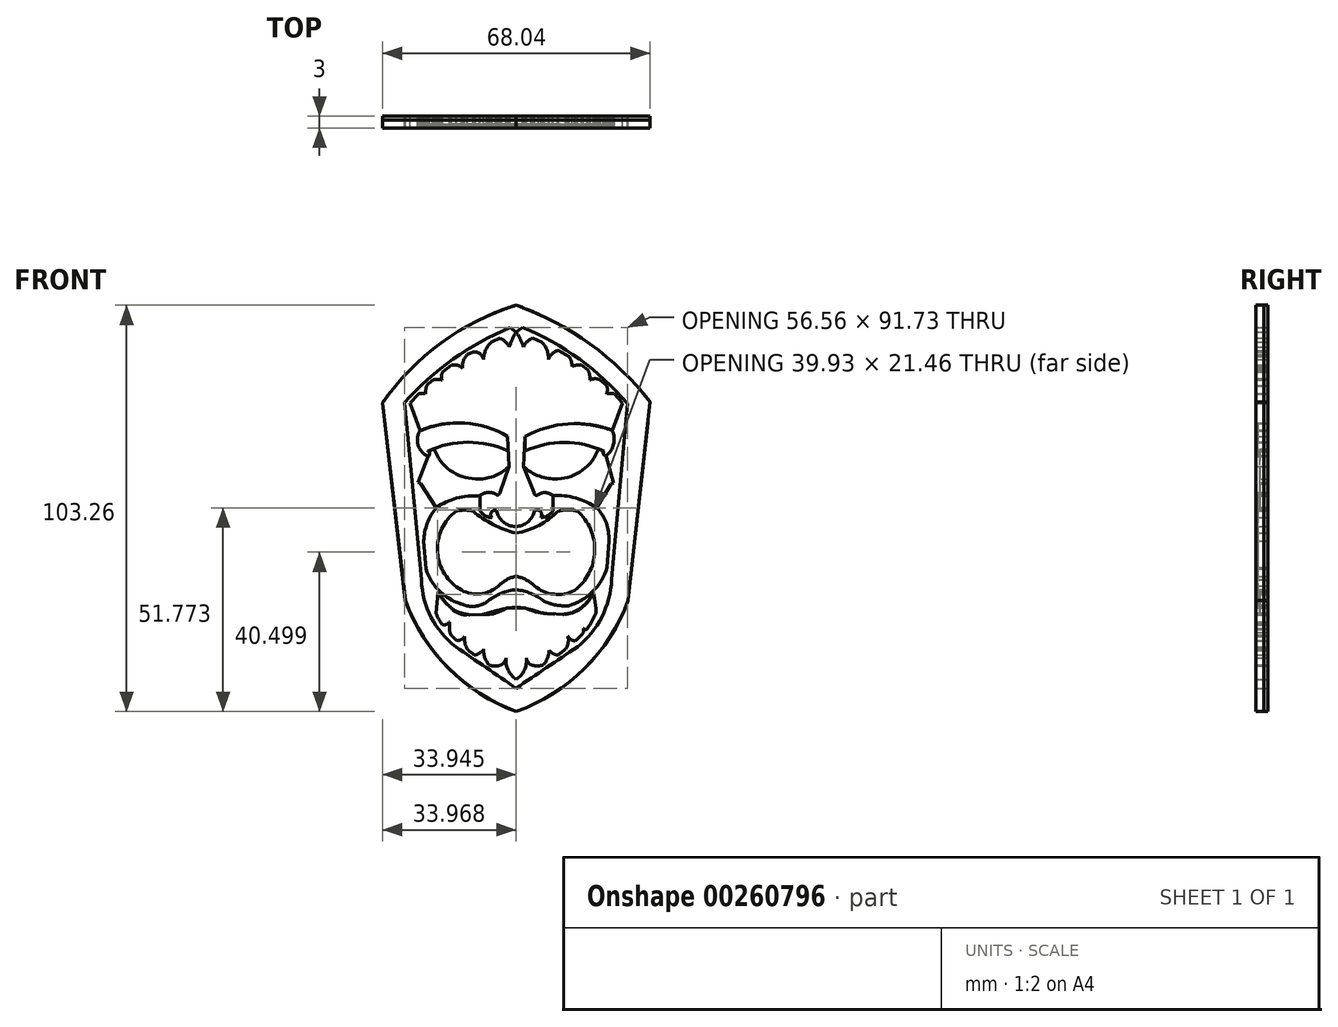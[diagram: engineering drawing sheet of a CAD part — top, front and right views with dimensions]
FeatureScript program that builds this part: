
annotation { "Feature Type Name" : "Feature", "Feature Type Description" : "" }
export const myFeature = defineFeature(function(context is Context, id is Id, definition is map)
    precondition{}
    {
        {
            var Q0;
            Q0=qCreatedBy(makeId("Front.planeOp"),FACE);
            var sketch = newSketch(context, id + "F0", { "sketchPlane" : qUnion([Q0])});
            skArc(sketch, "E0", {"start": v(34.06, 21.35) * mm, "mid": v(18.81, 36.12) * mm, "end": v(0, 45.95) * mm});
            skArc(sketch, "E1", {"start": v(0, 45.95) * mm, "mid": v(-19.06, 36.4) * mm, "end": v(-33.95, 21.15) * mm});
            skLineSegment(sketch, "E2", {"start": v(-33.95, 21.15) * mm, "end": v(-28.15, -29.05) * mm});
            skLineSegment(sketch, "E3", {"start": v(34.06, 21.35) * mm, "end": v(28.46, -29.05) * mm});
            skArc(sketch, "E4", {"start": v(-28.15, -29.05) * mm, "mid": v(-17.17, -46.24) * mm, "end": v(0, -57.26) * mm});
            skArc(sketch, "E5", {"start": v(0, -57.26) * mm, "mid": v(17.38, -46.33) * mm, "end": v(28.46, -29.05) * mm});
            skArc(sketch, "E6", {"start": v(-4.95, -6.25) * mm, "mid": v(-0.14, -10.26) * mm, "end": v(4.66, -6.25) * mm});
            skArc(sketch, "E7", {"start": v(-4.95, -6.25) * mm, "mid": v(-6.28, -6.6) * mm, "end": v(-6.16, -7.97) * mm});
            skArc(sketch, "E8", {"start": v(6.32, -7.94) * mm, "mid": v(6.17, -6.43) * mm, "end": v(4.66, -6.25) * mm});
            skArc(sketch, "E9", {"start": v(6.32, -7.94) * mm, "mid": v(8.06, -7.52) * mm, "end": v(9.33, -6.25) * mm});
            skArc(sketch, "E10", {"start": v(-9.24, -5.96) * mm, "mid": v(-8.02, -7.45) * mm, "end": v(-6.16, -7.97) * mm});
            skLineSegment(sketch, "E11", {"start": v(-9.24, -5.96) * mm, "end": v(-9.24, -2.5) * mm});
            skLineSegment(sketch, "E12", {"start": v(9.33, -6.25) * mm, "end": v(9.33, -2.5) * mm});
            skArc(sketch, "E13", {"start": v(-5.2, -2) * mm, "mid": v(-7.3, -1.58) * mm, "end": v(-9.24, -2.5) * mm});
            skArc(sketch, "E14", {"start": v(9.33, -2.5) * mm, "mid": v(7.6, -1.66) * mm, "end": v(5.72, -2.07) * mm});
            skArc(sketch, "E15", {"start": v(-5.2, -2) * mm, "mid": v(-4.5, -2.22) * mm, "end": v(-4.15, -1.58) * mm});
            skPoint(sketch, "E15.endSnap0", {"position": v(-7.3, -1.58) * mm});
            skArc(sketch, "E16", {"start": v(4.48, -1.6) * mm, "mid": v(4.93, -2.29) * mm, "end": v(5.72, -2.07) * mm});
            skLineSegment(sketch, "E17", {"start": v(-4.15, -1.58) * mm, "end": v(-1.86, 4.97) * mm});
            skLineSegment(sketch, "E18", {"start": v(4.48, -1.6) * mm, "end": v(1.89, 4.97) * mm});
            skLineSegment(sketch, "E19", {"start": v(1.89, 4.97) * mm, "end": v(3.01, 28.05) * mm});
            skLineSegment(sketch, "E20", {"start": v(-1.86, 4.97) * mm, "end": v(-2.83, 28.05) * mm});
            skArc(sketch, "E21", {"start": v(0, 39.14) * mm, "mid": v(-2.23, 33.8) * mm, "end": v(-2.83, 28.05) * mm});
            skArc(sketch, "E22", {"start": v(3.01, 28.05) * mm, "mid": v(2.38, 33.83) * mm, "end": v(0, 39.14) * mm});
            skArc(sketch, "E23", {"start": v(0, 39.14) * mm, "mid": v(-14.68, 31.95) * mm, "end": v(-26.96, 21.15) * mm});
            skArc(sketch, "E24", {"start": v(27.07, 21.15) * mm, "mid": v(14.78, 32.02) * mm, "end": v(0, 39.14) * mm});
            skArc(sketch, "E25", {"start": v(-18.2, -36.17) * mm, "mid": v(-9.75, -43.53) * mm, "end": v(0, -49.05) * mm});
            skArc(sketch, "E26", {"start": v(0, -49.05) * mm, "mid": v(9.75, -43.55) * mm, "end": v(18.15, -36.17) * mm});
            skArc(sketch, "E27", {"start": v(-22.54, -25.68) * mm, "mid": v(-20.91, -31.15) * mm, "end": v(-18.2, -36.17) * mm});
            skArc(sketch, "E28", {"start": v(18.15, -36.17) * mm, "mid": v(20.78, -31.11) * mm, "end": v(22.5, -25.68) * mm});
            skLineSegment(sketch, "E29", {"start": v(-26.96, 21.15) * mm, "end": v(-22.54, -25.68) * mm});
            skLineSegment(sketch, "E30", {"start": v(22.5, -25.68) * mm, "end": v(27.07, 21.15) * mm});
            skArc(sketch, "E31", {"start": v(-1.76, 35.38) * mm, "mid": v(-2.77, 36.68) * mm, "end": v(-4.14, 37.59) * mm});
            skArc(sketch, "E32", {"start": v(-6.23, 36.67) * mm, "mid": v(-7.72, 34.63) * mm, "end": v(-8.3, 32.17) * mm});
            skArc(sketch, "E33", {"start": v(4.2, 37.6) * mm, "mid": v(2.83, 36.72) * mm, "end": v(1.89, 35.38) * mm});
            skArc(sketch, "E34", {"start": v(8.18, 32.17) * mm, "mid": v(7.82, 34.58) * mm, "end": v(6.5, 36.63) * mm});
            skArc(sketch, "E35", {"start": v(10.73, 34.49) * mm, "mid": v(9.16, 33.65) * mm, "end": v(8.18, 32.17) * mm});
            skArc(sketch, "E36", {"start": v(14.13, 30.4) * mm, "mid": v(14.02, 31.7) * mm, "end": v(13.44, 32.88) * mm});
            skArc(sketch, "E37", {"start": v(-12.43, 33.38) * mm, "mid": v(-13.4, 31.84) * mm, "end": v(-13.67, 30.04) * mm});
            skArc(sketch, "E38", {"start": v(-8.3, 32.17) * mm, "mid": v(-9.23, 33.64) * mm, "end": v(-10.91, 34.08) * mm});
            skArc(sketch, "E39", {"start": v(-13.67, 30.04) * mm, "mid": v(-14.96, 30.72) * mm, "end": v(-16.41, 30.75) * mm});
            skArc(sketch, "E40", {"start": v(16.61, 30.75) * mm, "mid": v(15.34, 30.75) * mm, "end": v(14.13, 30.4) * mm});
            skArc(sketch, "E41", {"start": v(18.72, 26.93) * mm, "mid": v(18.67, 28.23) * mm, "end": v(18.3, 29.49) * mm});
            skArc(sketch, "E42", {"start": v(21.38, 26.93) * mm, "mid": v(20.05, 27.3) * mm, "end": v(18.72, 26.93) * mm});
            skArc(sketch, "E43", {"start": v(22.97, 23.47) * mm, "mid": v(23.18, 24.43) * mm, "end": v(23.05, 25.4) * mm});
            skArc(sketch, "E44", {"start": v(24.97, 23.47) * mm, "mid": v(23.97, 23.54) * mm, "end": v(22.97, 23.47) * mm});
            skArc(sketch, "E45", {"start": v(-18.68, 29.04) * mm, "mid": v(-18.98, 28) * mm, "end": v(-18.84, 26.93) * mm});
            skArc(sketch, "E46", {"start": v(-18.84, 26.93) * mm, "mid": v(-20.02, 27.15) * mm, "end": v(-21.2, 26.93) * mm});
            skArc(sketch, "E47", {"start": v(-22.77, 25.5) * mm, "mid": v(-22.94, 24.5) * mm, "end": v(-23, 23.47) * mm});
            skArc(sketch, "E48", {"start": v(-23, 23.47) * mm, "mid": v(-23.92, 23.54) * mm, "end": v(-24.84, 23.47) * mm});
            skLineSegment(sketch, "E49", {"start": v(-8.3, 32.17) * mm, "end": v(-6.65, 14.76) * mm});
            skLineSegment(sketch, "E50", {"start": v(-13.67, 30.04) * mm, "end": v(-11.48, 15.83) * mm});
            skLineSegment(sketch, "E51", {"start": v(-18.84, 26.93) * mm, "end": v(-16.08, 15.97) * mm});
            skLineSegment(sketch, "E52", {"start": v(-23, 23.47) * mm, "end": v(-19.76, 15.55) * mm});
            skLineSegment(sketch, "E53", {"start": v(-26.96, 21.15) * mm, "end": v(-24.42, 14.13) * mm});
            skLineSegment(sketch, "E54", {"start": v(8.18, 32.17) * mm, "end": v(6.26, 14.4) * mm});
            skLineSegment(sketch, "E55", {"start": v(14.13, 30.4) * mm, "end": v(11.16, 15.6) * mm});
            skLineSegment(sketch, "E56", {"start": v(18.72, 26.93) * mm, "end": v(15.97, 15.87) * mm});
            skLineSegment(sketch, "E57", {"start": v(22.97, 23.47) * mm, "end": v(20.08, 15.43) * mm});
            skLineSegment(sketch, "E58", {"start": v(27.07, 21.15) * mm, "end": v(24.52, 14.2) * mm});
            skArc(sketch, "E59", {"start": v(-2.18, 12.64) * mm, "mid": v(-13.13, 16) * mm, "end": v(-24.42, 14.13) * mm});
            skArc(sketch, "E60", {"start": v(24.52, 14.2) * mm, "mid": v(13.22, 15.82) * mm, "end": v(2.26, 12.63) * mm});
            skLineSegment(sketch, "E61", {"start": v(-19.8, -26.85) * mm, "end": v(-20.4, -32.31) * mm});
            skLineSegment(sketch, "E62", {"start": v(-16.98, -30.48) * mm, "end": v(-16.98, -36.07) * mm});
            skArc(sketch, "E63", {"start": v(-16.98, -36.07) * mm, "mid": v(-16.88, -36.96) * mm, "end": v(-16.6, -37.8) * mm});
            skArc(sketch, "E64", {"start": v(-15.13, -39.2) * mm, "mid": v(-13.97, -39) * mm, "end": v(-13.1, -38.2) * mm});
            skLineSegment(sketch, "E65", {"start": v(-13.1, -38.2) * mm, "end": v(-12.59, -32.7) * mm});
            skArc(sketch, "E66", {"start": v(-13.1, -38.2) * mm, "mid": v(-12.99, -39.95) * mm, "end": v(-12.34, -41.58) * mm});
            skArc(sketch, "E67", {"start": v(-10.57, -42.94) * mm, "mid": v(-9.24, -42.41) * mm, "end": v(-8.23, -41.4) * mm});
            skLineSegment(sketch, "E68", {"start": v(-8.23, -41.4) * mm, "end": v(-7.66, -32.61) * mm});
            skLineSegment(sketch, "E69", {"start": v(-7.66, -32.61) * mm, "end": v(-12.59, -32.7) * mm});
            skArc(sketch, "E70", {"start": v(-19.8, -26.85) * mm, "mid": v(-18.63, -28.85) * mm, "end": v(-16.98, -30.48) * mm});
            skArc(sketch, "E71", {"start": v(-16.98, -30.48) * mm, "mid": v(-15.06, -32.14) * mm, "end": v(-12.59, -32.7) * mm});
            skArc(sketch, "E72", {"start": v(-7.66, -32.61) * mm, "mid": v(-4.85, -32.15) * mm, "end": v(-2.3, -30.9) * mm});
            skLineSegment(sketch, "E73", {"start": v(-2.3, -30.9) * mm, "end": v(2.2, -30.9) * mm});
            skArc(sketch, "E74", {"start": v(2.2, -30.9) * mm, "mid": v(4.96, -31.92) * mm, "end": v(7.88, -32.38) * mm});
            skLineSegment(sketch, "E75", {"start": v(7.88, -32.38) * mm, "end": v(12.54, -32.64) * mm});
            skArc(sketch, "E76", {"start": v(12.54, -32.64) * mm, "mid": v(16.9, -30.74) * mm, "end": v(19.69, -26.9) * mm});
            skLineSegment(sketch, "E77", {"start": v(19.69, -26.9) * mm, "end": v(20.28, -31.01) * mm});
            skArc(sketch, "E78", {"start": v(20.28, -32.26) * mm, "mid": v(20.33, -31.64) * mm, "end": v(20.28, -31.01) * mm});
            skArc(sketch, "E79", {"start": v(17.15, -36.17) * mm, "mid": v(17.65, -36.47) * mm, "end": v(18.15, -36.17) * mm});
            skArc(sketch, "E80", {"start": v(13.1, -38.04) * mm, "mid": v(13.86, -38.97) * mm, "end": v(15, -39.3) * mm});
            skArc(sketch, "E81", {"start": v(12.7, -41.3) * mm, "mid": v(13.23, -39.71) * mm, "end": v(13.1, -38.04) * mm});
            skArc(sketch, "E82", {"start": v(8.39, -41.7) * mm, "mid": v(9.37, -42.55) * mm, "end": v(10.6, -42.94) * mm});
            skArc(sketch, "E83", {"start": v(6.97, -45.4) * mm, "mid": v(7.95, -43.66) * mm, "end": v(8.39, -41.7) * mm});
            skLineSegment(sketch, "E84", {"start": v(13.1, -38.04) * mm, "end": v(12.54, -32.64) * mm});
            skLineSegment(sketch, "E85", {"start": v(17.15, -36.17) * mm, "end": v(16.9, -30.74) * mm});
            skLineSegment(sketch, "E86", {"start": v(17.15, -36.17) * mm, "end": v(17.15, -37.22) * mm});
            skArc(sketch, "E87", {"start": v(3.8, -45.4) * mm, "mid": v(5.38, -45.7) * mm, "end": v(6.97, -45.4) * mm});
            skArc(sketch, "E88", {"start": v(2.59, -43.7) * mm, "mid": v(3, -44.68) * mm, "end": v(3.8, -45.4) * mm});
            skArc(sketch, "E89", {"start": v(0, -49.05) * mm, "mid": v(2.1, -46.76) * mm, "end": v(2.59, -43.7) * mm});
            skArc(sketch, "E90", {"start": v(-2.58, -43.7) * mm, "mid": v(-2.04, -46.73) * mm, "end": v(0, -49.05) * mm});
            skArc(sketch, "E91", {"start": v(-3.72, -45.37) * mm, "mid": v(-2.96, -44.66) * mm, "end": v(-2.58, -43.7) * mm});
            skArc(sketch, "E92", {"start": v(-7, -45.37) * mm, "mid": v(-5.36, -45.72) * mm, "end": v(-3.72, -45.37) * mm});
            skArc(sketch, "E93", {"start": v(-8.23, -41.4) * mm, "mid": v(-7.98, -43.5) * mm, "end": v(-7, -45.37) * mm});
            skLineSegment(sketch, "E94", {"start": v(-2.58, -43.7) * mm, "end": v(-2.3, -30.9) * mm});
            skLineSegment(sketch, "E95", {"start": v(2.59, -43.7) * mm, "end": v(2.2, -30.9) * mm});
            skLineSegment(sketch, "E96", {"start": v(8.39, -41.7) * mm, "end": v(7.88, -32.38) * mm});
            skArc(sketch, "E97", {"start": v(0, -51.37) * mm, "mid": v(-7.64, -46.1) * mm, "end": v(-15.29, -40.85) * mm});
            skArc(sketch, "E98", {"start": v(15.54, -40.85) * mm, "mid": v(7.76, -46.1) * mm, "end": v(0, -51.37) * mm});
            skArc(sketch, "E99", {"start": v(-24.05, -23.86) * mm, "mid": v(-21.6, -33.35) * mm, "end": v(-15.29, -40.85) * mm});
            skArc(sketch, "E100", {"start": v(15.54, -40.85) * mm, "mid": v(21.77, -33.25) * mm, "end": v(24.24, -23.74) * mm});
            skLineSegment(sketch, "E101", {"start": v(-28.32, 21.26) * mm, "end": v(-24.05, -23.86) * mm});
            skLineSegment(sketch, "E102", {"start": v(28.25, 21) * mm, "end": v(24.24, -23.74) * mm});
            skArc(sketch, "E103", {"start": v(-1.57, 40.24) * mm, "mid": v(-16.02, 32.26) * mm, "end": v(-28.32, 21.26) * mm});
            skArc(sketch, "E104", {"start": v(28.25, 21) * mm, "mid": v(16.05, 32.24) * mm, "end": v(1.6, 40.36) * mm});
            skLineSegment(sketch, "E105", {"start": v(0, 39.14) * mm, "end": v(-1.57, 40.24) * mm});
            skLineSegment(sketch, "E106", {"start": v(0, 39.14) * mm, "end": v(1.6, 40.36) * mm});
            skLineSegment(sketch, "E107", {"start": v(-26.96, 21.15) * mm, "end": v(-24.84, 23.47) * mm});
            skLineSegment(sketch, "E108", {"start": v(-22.77, 25.5) * mm, "end": v(-21.2, 26.93) * mm});
            skLineSegment(sketch, "E109", {"start": v(-18.68, 29.04) * mm, "end": v(-16.41, 30.75) * mm});
            skLineSegment(sketch, "E110", {"start": v(-12.43, 33.38) * mm, "end": v(-10.91, 34.08) * mm});
            skLineSegment(sketch, "E111", {"start": v(-6.23, 36.67) * mm, "end": v(-4.14, 37.59) * mm});
            skLineSegment(sketch, "E112", {"start": v(4.2, 37.6) * mm, "end": v(6.5, 36.63) * mm});
            skLineSegment(sketch, "E113", {"start": v(10.73, 34.49) * mm, "end": v(13.44, 32.88) * mm});
            skLineSegment(sketch, "E114", {"start": v(16.61, 30.75) * mm, "end": v(18.3, 29.49) * mm});
            skLineSegment(sketch, "E115", {"start": v(21.38, 26.93) * mm, "end": v(23.05, 25.4) * mm});
            skLineSegment(sketch, "E116", {"start": v(24.97, 23.47) * mm, "end": v(27.07, 21.15) * mm});
            skArc(sketch, "E117", {"start": v(-18.91, -35.05) * mm, "mid": v(-17.83, -35.18) * mm, "end": v(-16.98, -34.49) * mm});
            skSolve(sketch);
        }
        {
            var Q0;
            Q0=qCreatedBy(makeId("Front.planeOp"),FACE);
            var sketch = newSketch(context, id + "F1", { "sketchPlane" : qUnion([Q0])});
            skArc(sketch, "E118", {"start": v(-2.16, 12.64) * mm, "mid": v(-13.16, 16) * mm, "end": v(-24.48, 14) * mm});
            skArc(sketch, "E119", {"start": v(24.36, 14.13) * mm, "mid": v(13.13, 15.82) * mm, "end": v(2.23, 12.64) * mm});
            skArc(sketch, "E120", {"start": v(22.87, 7.79) * mm, "mid": v(24.77, 10.69) * mm, "end": v(24.36, 14.13) * mm});
            skArc(sketch, "E121", {"start": v(-24.48, 14) * mm, "mid": v(-24.87, 10.32) * mm, "end": v(-22.4, 7.58) * mm});
            skArc(sketch, "E122", {"start": v(-22.4, 7.58) * mm, "mid": v(-21.99, 8.22) * mm, "end": v(-22.4, 8.86) * mm});
            skArc(sketch, "E123", {"start": v(22.27, 8.86) * mm, "mid": v(22.21, 8.13) * mm, "end": v(22.87, 7.79) * mm});
            skArc(sketch, "E124", {"start": v(22.27, 8.86) * mm, "mid": v(12.25, 11.1) * mm, "end": v(2.23, 8.86) * mm});
            skArc(sketch, "E125", {"start": v(-1.95, 8.86) * mm, "mid": v(-12.17, 11.15) * mm, "end": v(-22.4, 8.86) * mm});
            skArc(sketch, "E126", {"start": v(-9.37, -2.54) * mm, "mid": v(-15.1, -3.05) * mm, "end": v(-20.3, -5.5) * mm});
            skArc(sketch, "E127", {"start": v(20.51, -5.57) * mm, "mid": v(15.15, -3.03) * mm, "end": v(9.25, -2.4) * mm});
            skArc(sketch, "E128", {"start": v(23.55, -13.87) * mm, "mid": v(22.9, -9.4) * mm, "end": v(20.51, -5.57) * mm});
            skArc(sketch, "E129", {"start": v(-20.3, -5.5) * mm, "mid": v(-22.6, -9.45) * mm, "end": v(-23.47, -13.94) * mm});
            skLineSegment(sketch, "E130", {"start": v(-23.47, -13.94) * mm, "end": v(-22.95, -21.1) * mm});
            skLineSegment(sketch, "E131", {"start": v(23.55, -13.87) * mm, "end": v(23.13, -20.68) * mm});
            skArc(sketch, "E132", {"start": v(-22.95, -21.1) * mm, "mid": v(-19.25, -26.83) * mm, "end": v(-13.3, -30.17) * mm});
            skArc(sketch, "E133", {"start": v(13.29, -30.39) * mm, "mid": v(19.46, -26.8) * mm, "end": v(23.13, -20.68) * mm});
            skArc(sketch, "E134", {"start": v(-13.3, -30.17) * mm, "mid": v(-10.14, -30.49) * mm, "end": v(-7.22, -29.24) * mm});
            skArc(sketch, "E135", {"start": v(7.14, -29.24) * mm, "mid": v(10.14, -30.22) * mm, "end": v(13.29, -30.39) * mm});
            skArc(sketch, "E136", {"start": v(0, -26.31) * mm, "mid": v(-3.83, -27.25) * mm, "end": v(-7.22, -29.24) * mm});
            skArc(sketch, "E137", {"start": v(7.14, -29.24) * mm, "mid": v(3.78, -27.28) * mm, "end": v(0, -26.31) * mm});
            skLineSegment(sketch, "E138", {"start": v(-9.37, -2.54) * mm, "end": v(-9.24, -2.55) * mm});
            skLineSegment(sketch, "E139", {"start": v(-9.24, -2.55) * mm, "end": v(-9.24, -5.94) * mm});
            skLineSegment(sketch, "E140", {"start": v(9.25, -2.4) * mm, "end": v(9.25, -6.32) * mm});
            skArc(sketch, "E141", {"start": v(-9.24, -5.94) * mm, "mid": v(-8.03, -7.45) * mm, "end": v(-6.16, -7.94) * mm});
            skArc(sketch, "E142", {"start": v(6.33, -7.93) * mm, "mid": v(8, -7.52) * mm, "end": v(9.25, -6.32) * mm});
            skArc(sketch, "E143", {"start": v(-4.95, -6.24) * mm, "mid": v(-6.26, -6.59) * mm, "end": v(-6.16, -7.94) * mm});
            skArc(sketch, "E144", {"start": v(6.33, -7.93) * mm, "mid": v(6.15, -6.43) * mm, "end": v(4.65, -6.24) * mm});
            skArc(sketch, "E145", {"start": v(-4.95, -6.24) * mm, "mid": v(-0.14, -10.24) * mm, "end": v(4.65, -6.24) * mm});
            skArc(sketch, "E146", {"start": v(-15.24, -6.32) * mm, "mid": v(-19.98, -16.74) * mm, "end": v(-13.9, -26.43) * mm});
            skArc(sketch, "E147", {"start": v(14.84, -26.5) * mm, "mid": v(19.96, -16.57) * mm, "end": v(15.52, -6.32) * mm});
            skArc(sketch, "E148", {"start": v(15.52, -6.32) * mm, "mid": v(13.12, -6.05) * mm, "end": v(10.73, -6.32) * mm});
            skArc(sketch, "E149", {"start": v(-11, -6.32) * mm, "mid": v(-13.12, -6.1) * mm, "end": v(-15.24, -6.32) * mm});
            skArc(sketch, "E150", {"start": v(-11, -6.32) * mm, "mid": v(-5.82, -9.76) * mm, "end": v(0, -11.92) * mm});
            skArc(sketch, "E151", {"start": v(0, -11.92) * mm, "mid": v(5.8, -9.95) * mm, "end": v(10.73, -6.32) * mm});
            skArc(sketch, "E152", {"start": v(-13.9, -26.43) * mm, "mid": v(-9, -27.35) * mm, "end": v(-4.45, -25.35) * mm});
            skArc(sketch, "E153", {"start": v(4.66, -25.35) * mm, "mid": v(9.58, -27.46) * mm, "end": v(14.84, -26.5) * mm});
            skArc(sketch, "E154", {"start": v(4.66, -25.35) * mm, "mid": v(2.5, -23.79) * mm, "end": v(0, -22.92) * mm});
            skArc(sketch, "E155", {"start": v(0, -22.92) * mm, "mid": v(-2.42, -23.78) * mm, "end": v(-4.45, -25.35) * mm});
            skLineSegment(sketch, "E156", {"start": v(-1.95, 8.86) * mm, "end": v(-2.16, 12.64) * mm});
            skLineSegment(sketch, "E157", {"start": v(2.23, 12.64) * mm, "end": v(2.23, 8.86) * mm});
            skSolve(sketch);
        }
        {
            var Q0;
            Q0=qCreatedBy(makeId("Front.planeOp"),FACE);
            var sketch = newSketch(context, id + "F2", { "sketchPlane" : qUnion([Q0])});
            skLineSegment(sketch, "E158", {"start": v(-20.36, -5.45) * mm, "end": v(-24.3, 0.63) * mm});
            skLineSegment(sketch, "E159", {"start": v(-24.3, 0.63) * mm, "end": v(-24.98, 0.95) * mm});
            skLineSegment(sketch, "E160", {"start": v(-24.98, 0.95) * mm, "end": v(-22.37, 7.54) * mm});
            skLineSegment(sketch, "E161", {"start": v(20.46, -5.55) * mm, "end": v(24.08, 0.5) * mm});
            skLineSegment(sketch, "E162", {"start": v(24.08, 0.5) * mm, "end": v(24.69, 0.82) * mm});
            skLineSegment(sketch, "E163", {"start": v(24.69, 0.82) * mm, "end": v(22.81, 7.73) * mm});
            skArc(sketch, "E164", {"start": v(22.24, 8.87) * mm, "mid": v(22.17, 8.12) * mm, "end": v(22.81, 7.73) * mm});
            skArc(sketch, "E165", {"start": v(-22.37, 7.54) * mm, "mid": v(-21.99, 8.18) * mm, "end": v(-22.37, 8.83) * mm});
            skArc(sketch, "E166", {"start": v(-9.3, -2.5) * mm, "mid": v(-15.07, -3.07) * mm, "end": v(-20.36, -5.45) * mm});
            skArc(sketch, "E167", {"start": v(20.46, -5.55) * mm, "mid": v(15.13, -3.08) * mm, "end": v(9.29, -2.44) * mm});
            skArc(sketch, "E168", {"start": v(9.29, -2.44) * mm, "mid": v(7.57, -1.65) * mm, "end": v(5.72, -2.07) * mm});
            skArc(sketch, "E169", {"start": v(4.49, -1.6) * mm, "mid": v(4.93, -2.3) * mm, "end": v(5.72, -2.07) * mm});
            skArc(sketch, "E170", {"start": v(-5.2, -2) * mm, "mid": v(-7.33, -1.6) * mm, "end": v(-9.3, -2.5) * mm});
            skArc(sketch, "E171", {"start": v(-5.2, -2) * mm, "mid": v(-4.5, -2.22) * mm, "end": v(-4.15, -1.59) * mm});
            skArc(sketch, "E172", {"start": v(1.9, 4.98) * mm, "mid": v(5.9, 2.53) * mm, "end": v(10.54, 1.85) * mm});
            skArc(sketch, "E173", {"start": v(10.54, 1.85) * mm, "mid": v(16.88, 4.06) * mm, "end": v(20.87, 9.44) * mm});
            skArc(sketch, "E174", {"start": v(-10.29, 1.85) * mm, "mid": v(-5.74, 2.5) * mm, "end": v(-1.86, 4.98) * mm});
            skArc(sketch, "E175", {"start": v(-20.86, 9.46) * mm, "mid": v(-16.76, 4.01) * mm, "end": v(-10.29, 1.85) * mm});
            skLineSegment(sketch, "E176", {"start": v(-22.37, 8.83) * mm, "end": v(-20.86, 9.46) * mm});
            skLineSegment(sketch, "E177", {"start": v(20.87, 9.44) * mm, "end": v(22.24, 8.87) * mm});
            skLineSegment(sketch, "E178", {"start": v(4.49, -1.6) * mm, "end": v(1.9, 4.98) * mm});
            skLineSegment(sketch, "E179", {"start": v(-1.86, 4.98) * mm, "end": v(-4.15, -1.59) * mm});
            skArc(sketch, "E180", {"start": v(-13.42, -32.37) * mm, "mid": v(-10.45, -32.78) * mm, "end": v(-7.48, -32.37) * mm});
            skArc(sketch, "E181", {"start": v(0, -30.76) * mm, "mid": v(-3.79, -31.36) * mm, "end": v(-7.48, -32.37) * mm});
            skArc(sketch, "E182", {"start": v(6.74, -32.37) * mm, "mid": v(3.43, -31.32) * mm, "end": v(0, -30.76) * mm});
            skArc(sketch, "E183", {"start": v(6.74, -32.37) * mm, "mid": v(9.97, -32.68) * mm, "end": v(13.2, -32.37) * mm});
            skArc(sketch, "E184", {"start": v(13.2, -32.37) * mm, "mid": v(17.15, -30.34) * mm, "end": v(19.64, -26.66) * mm});
            skArc(sketch, "E185", {"start": v(13.3, -30.38) * mm, "mid": v(16.72, -28.95) * mm, "end": v(19.64, -26.66) * mm});
            skArc(sketch, "E186", {"start": v(7.14, -29.26) * mm, "mid": v(10.15, -30.21) * mm, "end": v(13.3, -30.38) * mm});
            skArc(sketch, "E187", {"start": v(7.14, -29.26) * mm, "mid": v(3.78, -27.28) * mm, "end": v(0, -26.31) * mm});
            skArc(sketch, "E188", {"start": v(0, -26.31) * mm, "mid": v(-3.84, -27.25) * mm, "end": v(-7.23, -29.26) * mm});
            skArc(sketch, "E189", {"start": v(-13.3, -30.17) * mm, "mid": v(-10.15, -30.5) * mm, "end": v(-7.23, -29.26) * mm});
            skArc(sketch, "E190", {"start": v(-19.4, -26.68) * mm, "mid": v(-17.2, -30.36) * mm, "end": v(-13.42, -32.37) * mm});
            skArc(sketch, "E191", {"start": v(-19.4, -26.68) * mm, "mid": v(-16.58, -28.83) * mm, "end": v(-13.3, -30.17) * mm});
            skSolve(sketch);
        }
        {
            var Q0;
            Q0=makeQuery(id+"F2.imprint","IMPRINT",FACE,{"disambiguationData":[TD([[makeQuery(id+"F2.imprint","IMPRINT",EDGE,{"derivedFrom":sQuery(id+"F2.wireOp",EDGE,"E158")}),-1.0]])]});
            var Q1;
            Q1=makeQuery(id+"F2.imprint","IMPRINT",FACE,{"disambiguationData":[TD([[makeQuery(id+"F2.imprint","IMPRINT",EDGE,{"derivedFrom":sQuery(id+"F2.wireOp",EDGE,"E161")}),1.0]])]});
            var Q2;
            Q2=makeQuery(id+"F2.imprint","IMPRINT",FACE,{"disambiguationData":[TD([[makeQuery(id+"F2.imprint","IMPRINT",EDGE,{"derivedFrom":sQuery(id+"F2.wireOp",EDGE,"E180")}),1.0]])]});
            extrude(context, id + "F3", {"entities" : qUnion([Q0, Q1, Q2]), "depth" : 2 * mm});
        }
        {
            var Q0;
            Q0=makeQuery(id+"F1.imprint","IMPRINT",FACE,{"disambiguationData":[TD([[makeQuery(id+"F1.imprint","IMPRINT",EDGE,{"derivedFrom":sQuery(id+"F1.wireOp",EDGE,"E126")}),1.0]])]});
            var Q1;
            Q1=makeQuery(id+"F1.imprint","IMPRINT",FACE,{"disambiguationData":[TD([[makeQuery(id+"F1.imprint","IMPRINT",EDGE,{"derivedFrom":sQuery(id+"F1.wireOp",EDGE,"E119")}),1.0]])]});
            var Q2;
            Q2=makeQuery(id+"F1.imprint","IMPRINT",FACE,{"disambiguationData":[TD([[makeQuery(id+"F1.imprint","IMPRINT",EDGE,{"derivedFrom":sQuery(id+"F1.wireOp",EDGE,"E118")}),1.0]])]});
            extrude(context, id + "F4", {"entities" : qUnion([Q0, Q1, Q2]), "depth" : 2.5 * mm});
        }
        {
            var Q0;
            Q0=makeQuery(id+"F0.imprint","IMPRINT",FACE,{"disambiguationData":[TD([[makeQuery(id+"F0.imprint","IMPRINT",EDGE,{"derivedFrom":sQuery(id+"F0.wireOp",EDGE,"E6")}),1.0]])]});
            var Q1;
            {var subQ3=sQuery(id+"F0.wireOp",EDGE,"E31");Q1=makeQuery(id+"F0.imprint","IMPRINT",FACE,{"disambiguationData":[TD([[makeQuery(id+"F0.imprint","IMPRINT",EDGE,{"derivedFrom":subQ3}),1.0]])]});}
            var Q2;
            {var subQ5=sQuery(id+"F0.wireOp",EDGE,"E39");Q2=makeQuery(id+"F0.imprint","IMPRINT",FACE,{"disambiguationData":[TD([[makeQuery(id+"F0.imprint","IMPRINT",EDGE,{"derivedFrom":subQ5}),1.0]])]});}
            var Q3;
            {var subQ5=sQuery(id+"F0.wireOp",EDGE,"E46");Q3=makeQuery(id+"F0.imprint","IMPRINT",FACE,{"disambiguationData":[TD([[makeQuery(id+"F0.imprint","IMPRINT",EDGE,{"derivedFrom":subQ5}),1.0]])]});}
            var Q4;
            {var subQ4=sQuery(id+"F0.wireOp",EDGE,"E48");Q4=makeQuery(id+"F0.imprint","IMPRINT",FACE,{"disambiguationData":[TD([[makeQuery(id+"F0.imprint","IMPRINT",EDGE,{"derivedFrom":subQ4}),1.0]])]});}
            var Q5;
            {var subQ0=sQuery(id+"F0.wireOp",EDGE,"E33");Q5=makeQuery(id+"F0.imprint","IMPRINT",FACE,{"disambiguationData":[TD([[makeQuery(id+"F0.imprint","IMPRINT",EDGE,{"derivedFrom":subQ0}),1.0]])]});}
            var Q6;
            Q6=makeQuery(id+"F0.imprint","IMPRINT",FACE,{"disambiguationData":[TD([[makeQuery(id+"F0.imprint","IMPRINT",EDGE,{"derivedFrom":sQuery(id+"F0.wireOp",EDGE,"E35")}),1.0]])]});
            var Q7;
            Q7=makeQuery(id+"F0.imprint","IMPRINT",FACE,{"disambiguationData":[TD([[makeQuery(id+"F0.imprint","IMPRINT",EDGE,{"derivedFrom":sQuery(id+"F0.wireOp",EDGE,"E40")}),1.0]])]});
            var Q8;
            Q8=makeQuery(id+"F0.imprint","IMPRINT",FACE,{"disambiguationData":[TD([[makeQuery(id+"F0.imprint","IMPRINT",EDGE,{"derivedFrom":sQuery(id+"F0.wireOp",EDGE,"E42")}),1.0]])]});
            var Q9;
            Q9=makeQuery(id+"F0.imprint","IMPRINT",FACE,{"disambiguationData":[TD([[makeQuery(id+"F0.imprint","IMPRINT",EDGE,{"derivedFrom":sQuery(id+"F0.wireOp",EDGE,"E44")}),1.0]])]});
            var Q10;
            {var subQ1=sQuery(id+"F0.wireOp",EDGE,"E61");Q10=makeQuery(id+"F0.imprint","IMPRINT",FACE,{"disambiguationData":[TD([[makeQuery(id+"F0.imprint","IMPRINT",EDGE,{"derivedFrom":subQ1}),1.0]])]});}
            var Q11;
            {var subQ0=sQuery(id+"F0.wireOp",EDGE,"E63");Q11=makeQuery(id+"F0.imprint","IMPRINT",FACE,{"disambiguationData":[TD([[makeQuery(id+"F0.imprint","IMPRINT",EDGE,{"derivedFrom":subQ0}),1.0]])]});}
            var Q12;
            Q12=makeQuery(id+"F0.imprint","IMPRINT",FACE,{"disambiguationData":[TD([[makeQuery(id+"F0.imprint","IMPRINT",EDGE,{"derivedFrom":sQuery(id+"F0.wireOp",EDGE,"E65")}),-1.0]])]});
            var Q13;
            Q13=makeQuery(id+"F0.imprint","IMPRINT",FACE,{"disambiguationData":[TD([[makeQuery(id+"F0.imprint","IMPRINT",EDGE,{"derivedFrom":sQuery(id+"F0.wireOp",EDGE,"E68")}),-1.0]])]});
            var Q14;
            Q14=makeQuery(id+"F0.imprint","IMPRINT",FACE,{"disambiguationData":[TD([[makeQuery(id+"F0.imprint","IMPRINT",EDGE,{"derivedFrom":sQuery(id+"F0.wireOp",EDGE,"E73")}),-1.0]])]});
            var Q15;
            Q15=makeQuery(id+"F0.imprint","IMPRINT",FACE,{"disambiguationData":[TD([[makeQuery(id+"F0.imprint","IMPRINT",EDGE,{"derivedFrom":sQuery(id+"F0.wireOp",EDGE,"E74")}),-1.0]])]});
            var Q16;
            Q16=makeQuery(id+"F0.imprint","IMPRINT",FACE,{"disambiguationData":[TD([[makeQuery(id+"F0.imprint","IMPRINT",EDGE,{"derivedFrom":sQuery(id+"F0.wireOp",EDGE,"E75")}),-1.0]])]});
            var Q17;
            {var subQ1=sQuery(id+"F0.wireOp",EDGE,"E80");Q17=makeQuery(id+"F0.imprint","IMPRINT",FACE,{"disambiguationData":[TD([[makeQuery(id+"F0.imprint","IMPRINT",EDGE,{"derivedFrom":subQ1}),1.0]])]});}
            var Q18;
            {var subQ0=sQuery(id+"F0.wireOp",EDGE,"E77");Q18=makeQuery(id+"F0.imprint","IMPRINT",FACE,{"disambiguationData":[TD([[makeQuery(id+"F0.imprint","IMPRINT",EDGE,{"derivedFrom":subQ0}),-1.0]])]});}
            var Q19;
            Q19=makeQuery(id+"F0.imprint","IMPRINT",FACE,{"disambiguationData":[TD([[makeQuery(id+"F0.imprint","IMPRINT",EDGE,{"derivedFrom":sQuery(id+"F0.wireOp",EDGE,"E0")}),1.0]])]});
            extrude(context, id + "F5", {"entities" : qUnion([Q0, Q1, Q2, Q3, Q4, Q5, Q6, Q7, Q8, Q9, Q10, Q11, Q12, Q13, Q14, Q15, Q16, Q17, Q18, Q19]), "depth" : 3 * mm});
        }
        {
            var Q0;
            Q0=qCreatedBy(makeId("Front.planeOp"),FACE);
            var sketch = newSketch(context, id + "F6", { "sketchPlane" : qUnion([Q0])});
            skArc(sketch, "E192", {"start": v(0, 45.98) * mm, "mid": v(-19.06, 36.38) * mm, "end": v(-33.98, 21.12) * mm});
            skArc(sketch, "E193", {"start": v(34.06, 21.38) * mm, "mid": v(18.79, 36.11) * mm, "end": v(0, 45.98) * mm});
            skArc(sketch, "E194", {"start": v(-28.19, -29.02) * mm, "mid": v(-17.23, -46.28) * mm, "end": v(0, -57.28) * mm});
            skArc(sketch, "E195", {"start": v(0, -57.28) * mm, "mid": v(17.4, -46.36) * mm, "end": v(28.47, -29.06) * mm});
            skLineSegment(sketch, "E196", {"start": v(-28.19, -29.02) * mm, "end": v(-33.98, 21.12) * mm});
            skLineSegment(sketch, "E197", {"start": v(28.47, -29.06) * mm, "end": v(34.06, 21.38) * mm});
            skSolve(sketch);
        }
        {
            var Q0;
            Q0 = qSketchRegion(id + "F6", true);
            extrude(context, id + "F7", {"entities" : qUnion([Q0]), "depth" : 1 * mm});
        }
    });
